# Revit family: CITY SPACE_XX
name_source: partatom
category: Doors
revit_build: Autodesk Revit 2017 (Build: 20181011_1645(x64)
units: mm (PartAtom-declared; Revit-internal decimal feet)

## family parameters
Always vertical = Yes
Cut with Voids When Loaded = No
Host = Wall
OmniClass Number = 23.30.10.00
OmniClass Title = Doors
Room Calculation Point = No
Shared = No

## types (1)
- CITY SPACE_XX
    Analytic Construction = <None>
    FRAME MATERIAL = <By Category>
    Function = Interior
    GLAZED MATERIAL = <By Category>
    Glass 24mm = No
    Glass 28mm = Yes
    Height = 3000 mm  [stored 9.84252 ft]
    LOCK = 0 mm  [stored 0 ft]
    MAX HEIGHT = 3000 mm  [stored 9.84252 ft]
    MAX PANEL HEIGHT = 3000 mm  [stored 9.84252 ft]
    MAX PANEL WIDTH = 1250 mm  [stored 4.10105 ft]
    MAX WIDTH = 2500 mm  [stored 8.2021 ft]
    OFFSET = 0 mm  [stored 0 ft]
    OVERALL FRAME HEIGHT = 3000 mm  [stored 9.84252 ft]
    OVERALL FRAME WIDTH = 2500 mm  [stored 8.2021 ft]
    PANEL HEIGHT = 2970 mm
    PANEL WIDTH = 1225 mm  [stored 4.01903 ft]
    Rough Height = 3000 mm  [stored 9.84252 ft]
    Rough Width = 2500 mm  [stored 8.2021 ft]
    TOLERANCE = 0 mm  [stored 0 ft]
    Thickness = 0 mm  [stored 0 ft]
    Wall Closure = By host
    Width = 2500 mm  [stored 8.2021 ft]

note: [stored X ft] marks values corroborated as IEEE doubles in the binary element streams (Revit-internal decimal feet)

## geometry (parser evidence)
native form markers: Sweep x15
no freeform markers — native parametric forms only
